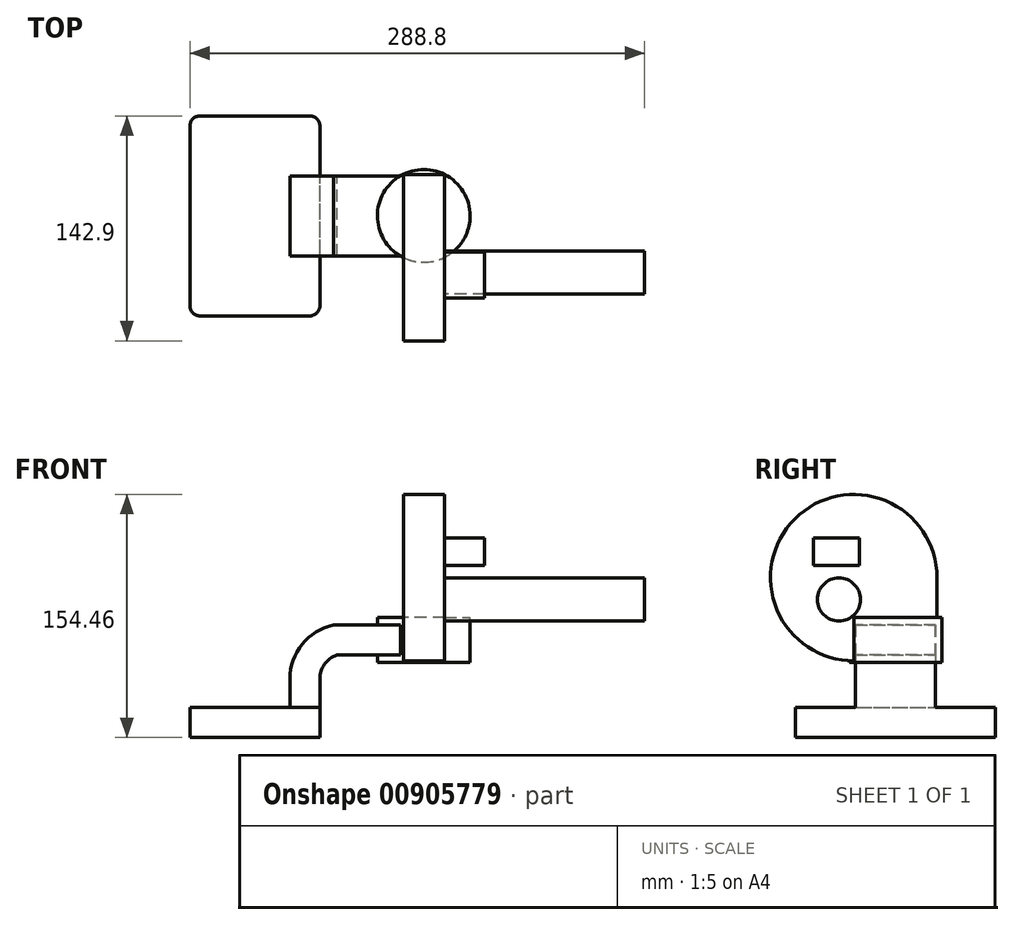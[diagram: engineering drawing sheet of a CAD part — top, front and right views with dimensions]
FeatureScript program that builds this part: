
annotation { "Feature Type Name" : "Feature", "Feature Type Description" : "" }
export const myFeature = defineFeature(function(context is Context, id is Id, definition is map)
    precondition{}
    {
        {
            var Q0;
            Q0=qCreatedBy(makeId("Front.planeOp"),FACE);
            var sketch = newSketch(context, id + "F0", { "sketchPlane" : qUnion([Q0])});
            skLineSegment(sketch, "E0.bottom", {"start": v(41.27, 9.53) * mm, "end": v(-41.27, 9.52) * mm});
            skLineSegment(sketch, "E0.top", {"start": v(41.28, -9.52) * mm, "end": v(-41.28, -9.53) * mm});
            skLineSegment(sketch, "E0.left", {"start": v(41.28, 9.53) * mm, "end": v(41.28, -9.52) * mm});
            skLineSegment(sketch, "E0.right", {"start": v(-41.28, 9.52) * mm, "end": v(-41.27, -9.53) * mm});
            skPoint(sketch, "E0.middle", {"position": v(0, 0) * mm});
            skLineSegment(sketch, "E1.bottom", {"start": v(85.93, 66.68) * mm, "end": v(136.73, 66.68) * mm});
            skLineSegment(sketch, "E1.top", {"start": v(85.93, 38.1) * mm, "end": v(136.73, 38.1) * mm});
            skLineSegment(sketch, "E1.left", {"start": v(85.93, 66.68) * mm, "end": v(85.93, 38.1) * mm});
            skLineSegment(sketch, "E1.right", {"start": v(136.73, 66.68) * mm, "end": v(136.73, 38.1) * mm});
            skPoint(sketch, "E1.middle", {"position": v(111.33, 52.39) * mm});
            skLineSegment(sketch, "E2", {"start": v(41.27, 9.53) * mm, "end": v(41.27, 27.77) * mm});
            skArc(sketch, "E3", {"start": v(41.28, 27.77) * mm, "mid": v(44.32, 37.11) * mm, "end": v(52.28, 42.88) * mm});
            skLineSegment(sketch, "E4", {"start": v(52.28, 42.88) * mm, "end": v(107.27, 42.88) * mm});
            skLineSegment(sketch, "E5.0", {"start": v(49.88, 61.93) * mm, "end": v(107.27, 61.93) * mm});
            skArc(sketch, "E5.1", {"start": v(22.23, 27.77) * mm, "mid": v(30, 49.74) * mm, "end": v(49.88, 61.93) * mm});
            skLineSegment(sketch, "E5.2", {"start": v(22.22, 9.53) * mm, "end": v(22.22, 27.77) * mm});
            skLineSegment(sketch, "E6", {"start": v(107.27, 66.68) * mm, "end": v(107.27, 38.1) * mm});
            skFitSpline(sketch, "E7", {"points": [v(-41.28, 9.53) * mm, v(49.88, 61.93) * mm], "startDerivative": vector(2, 125.65) * mm, "endDerivative": vector(111.48, 5) * mm});
            skSolve(sketch);
        }
        {
            var Q0;
            Q0=makeQuery(id+"F0.imprint","IMPRINT",FACE,{"disambiguationData":[TD([[makeQuery(id+"F0.imprint","IMPRINT",EDGE,{"derivedFrom":sQuery(id+"F0.wireOp",EDGE,"E0.top")}),-1.0]])]});
            extrude(context, id + "F1", {"entities" : qUnion([Q0]), "depth" : 127 * mm, "offsetDistance" : 25.4 * mm, "symmetric" : true});
        }
        {
            var Q0;
            {var subQ1=sQuery(id+"F0.wireOp",EDGE,"E2");Q0=makeQuery(id+"F0.imprint","IMPRINT",FACE,{"disambiguationData":[TD([[makeQuery(id+"F0.imprint","IMPRINT",EDGE,{"derivedFrom":subQ1}),1.0]])]});}
            var Q1;
            {var subQ0=sQuery(id+"F0.wireOp",EDGE,"E5.0");var subQ1=sQuery(id+"F0.wireOp",EDGE,"E1.left");var subQ2=makeQuery(id+"F0.imprint","INTERSECT",VERTEX,{"derivedFrom":[subQ1,subQ0]});Q1=makeQuery(id+"F0.imprint","IMPRINT",FACE,{"disambiguationData":[TD([[makeQuery(id+"F0.imprint","IMPRINT",EDGE,{"disambiguationData":[TD([[subQ2,-1.0]])],"derivedFrom":subQ1}),1.0]])]});}
            extrude(context, id + "F2", {"entities" : qUnion([Q0, Q1]), "operationType" : NewBodyOperationType.ADD, "depth" : 50.8 * mm, "offsetDistance" : 25.4 * mm, "symmetric" : true});
        }
        {
            var Q0;
            Q0=makeQuery(id+"F0.imprint","IMPRINT",FACE,{"disambiguationData":[TD([[makeQuery(id+"F0.imprint","IMPRINT",EDGE,{"derivedFrom":sQuery(id+"F0.wireOp",EDGE,"E5.1")}),1.0]])]});
            extrude(context, id + "F3", {"entities" : qUnion([Q0]), "operationType" : NewBodyOperationType.ADD, "depth" : 15.88 * mm, "offsetDistance" : 25.4 * mm, "symmetric" : true});
        }
        {
            var Q0;
            {var subQ0=sQuery(id+"F0.wireOp",EDGE,"E1.right");Q0=makeQuery(id+"F0.imprint","IMPRINT",FACE,{"disambiguationData":[TD([[makeQuery(id+"F0.imprint","IMPRINT",EDGE,{"derivedFrom":subQ0}),-1.0]])]});}
            var Q1;
            Q1=sQuery(id+"F0.wireOp",EDGE,"E6");
            revolve(context, id + "F4", {"operationType" : NewBodyOperationType.ADD, "surfaceOperationType" : NewSurfaceOperationType.NEW, "entities" : qUnion([Q0]), "axis" : qUnion([Q1]), "revolveType" : RevolveType.FULL});
        }
        {
            var Q0;
            Q0=makeQuery(id+"F1.opExtrude","CAP_EDGE",EDGE,{"disambiguationData":[OSD([sQuery(id+"F0.wireOp",EDGE,"E0.left")])],"isStart":false});
            var Q1;
            Q1=makeQuery(id+"F1.opExtrude","CAP_EDGE",EDGE,{"disambiguationData":[OSD([sQuery(id+"F0.wireOp",EDGE,"E0.left")])],"isStart":true});
            var Q2;
            Q2=makeQuery(id+"F1.opExtrude","CAP_EDGE",EDGE,{"disambiguationData":[OSD([sQuery(id+"F0.wireOp",EDGE,"E0.right")])],"isStart":true});
            var Q3;
            Q3=makeQuery(id+"F1.opExtrude","CAP_EDGE",EDGE,{"disambiguationData":[OSD([sQuery(id+"F0.wireOp",EDGE,"E0.right")])],"isStart":false});
            fillet(context, id + "F5", {"entities" : qUnion([Q0, Q1, Q2, Q3]), "radius" : 6.35 * mm, "tangentPropagation" : true, "allowEdgeOverflow" : false});
        }
        {
            var Q0;
            Q0=makeQuery(id+"F4.opRevolve","SWEPT_FACE",FACE,{"disambiguationData":[OSD([sQuery(id+"F0.wireOp",EDGE,"E1.bottom")])]});
            var sketch = newSketch(context, id + "F6", { "sketchPlane" : qUnion([Q0])});
            skLineSegment(sketch, "E8.bottom", {"start": v(120.53, 26.3) * mm, "end": v(94.5, 26.3) * mm});
            skLineSegment(sketch, "E8.top", {"start": v(120.53, -26.55) * mm, "end": v(94.5, -26.55) * mm});
            skLineSegment(sketch, "E8.left", {"start": v(120.53, 26.3) * mm, "end": v(120.53, -26.55) * mm});
            skLineSegment(sketch, "E8.right", {"start": v(94.5, 26.3) * mm, "end": v(94.5, -26.55) * mm});
            skSolve(sketch);
        }
        {
            var Q0;
            Q0 = qSketchRegion(id + "F6", true);
            extrude(context, id + "F7", {"entities" : qUnion([Q0]), "operationType" : NewBodyOperationType.ADD, "depth" : 25.4 * mm, "offsetDistance" : 25.4 * mm});
        }
        {
            var Q0;
            Q0=makeQuery(id+"F7.opExtrude","CAP_FACE",FACE,{"disambiguationData":[OSD([sQuery(id+"F6.wireOp",EDGE,"E8.bottom"),sQuery(id+"F6.wireOp",EDGE,"E8.top"),sQuery(id+"F6.wireOp",EDGE,"E8.left"),sQuery(id+"F6.wireOp",EDGE,"E8.right")])],"isStart":false});
            var Q1;
            Q1=makeQuery(id+"F7.opExtrude","CAP_EDGE",EDGE,{"disambiguationData":[OSD([sQuery(id+"F6.wireOp",EDGE,"E8.top")])],"isStart":false});
            revolve(context, id + "F8", {"operationType" : NewBodyOperationType.ADD, "surfaceOperationType" : NewSurfaceOperationType.NEW, "entities" : qUnion([Q0]), "axis" : qUnion([Q1]), "revolveType" : RevolveType.FULL});
        }
        {
            var Q0;
            {var subQ0=sQuery(id+"F6.wireOp",EDGE,"E8.left");Q0=makeQuery(id+"F8.boolean.opBoolean","MERGE",FACE,{"derivedFrom":[makeQuery(id+"F7.opExtrude","SWEPT_FACE",FACE,{"disambiguationData":[OSD([subQ0])]}),makeQuery(id+"F8.opRevolve","SWEPT_FACE",FACE,{"disambiguationData":[OSD([subQ0])]})]});}
            var sketch = newSketch(context, id + "F9", { "sketchPlane" : qUnion([Q0])});
            skLineSegment(sketch, "E9.bottom", {"start": v(-52.15, 117.34) * mm, "end": v(-22.93, 117.34) * mm});
            skLineSegment(sketch, "E9.top", {"start": v(-52.15, 99.73) * mm, "end": v(-22.93, 99.73) * mm});
            skLineSegment(sketch, "E9.left", {"start": v(-52.15, 117.34) * mm, "end": v(-52.15, 99.73) * mm});
            skLineSegment(sketch, "E9.right", {"start": v(-22.93, 117.34) * mm, "end": v(-22.93, 99.73) * mm});
            skSolve(sketch);
        }
        {
            var Q0;
            Q0=makeQuery(id+"F9.imprint","IMPRINT",FACE,{"disambiguationData":[TD([[makeQuery(id+"F9.imprint","IMPRINT",EDGE,{"derivedFrom":sQuery(id+"F9.wireOp",EDGE,"E9.bottom")}),-1.0]])]});
            extrude(context, id + "F10", {"entities" : qUnion([Q0]), "operationType" : NewBodyOperationType.ADD, "depth" : 25.4 * mm, "offsetDistance" : 25.4 * mm});
        }
        {
            var Q0;
            Q0=makeQuery(id+"F10.opExtrude","SWEPT_FACE",FACE,{"disambiguationData":[OSD([sQuery(id+"F9.wireOp",EDGE,"E9.bottom")])]});
            var sketch = newSketch(context, id + "F11", { "sketchPlane" : qUnion([Q0])});
            skCircle(sketch, "E10", {"center": v(132.34, -37.54) * mm, "radius": 6.35 * mm});
            skPoint(sketch, "E10.centerSnap0", {"position": v(120.53, -37.54) * mm});
            skSolve(sketch);
        }
        {
            var Q0;
            {var subQ0=sQuery(id+"F6.wireOp",EDGE,"E8.left");Q0=makeQuery(id+"F8.boolean.opBoolean","MERGE",FACE,{"derivedFrom":[makeQuery(id+"F7.opExtrude","SWEPT_FACE",FACE,{"disambiguationData":[OSD([subQ0])]}),makeQuery(id+"F8.opRevolve","SWEPT_FACE",FACE,{"disambiguationData":[OSD([subQ0])]})]});}
            var sketch = newSketch(context, id + "F12", { "sketchPlane" : qUnion([Q0])});
            skCircle(sketch, "E11", {"center": v(-35.97, 78.17) * mm, "radius": 13.68 * mm});
            skSolve(sketch);
        }
        {
            var Q0;
            Q0 = qSketchRegion(id + "F12", true);
            var Q1;
            Q1=makeQuery(id+"F12.imprint","IMPRINT",FACE,{"disambiguationData":[TD([[makeQuery(id+"F12.imprint","IMPRINT",EDGE,{"derivedFrom":sQuery(id+"F12.wireOp",EDGE,"E11")}),1.0]])]});
            extrude(context, id + "F13", {"entities" : qUnion([Q0, Q1]), "operationType" : NewBodyOperationType.ADD, "depth" : 127 * mm, "offsetDistance" : 25.4 * mm});
        }
    });
